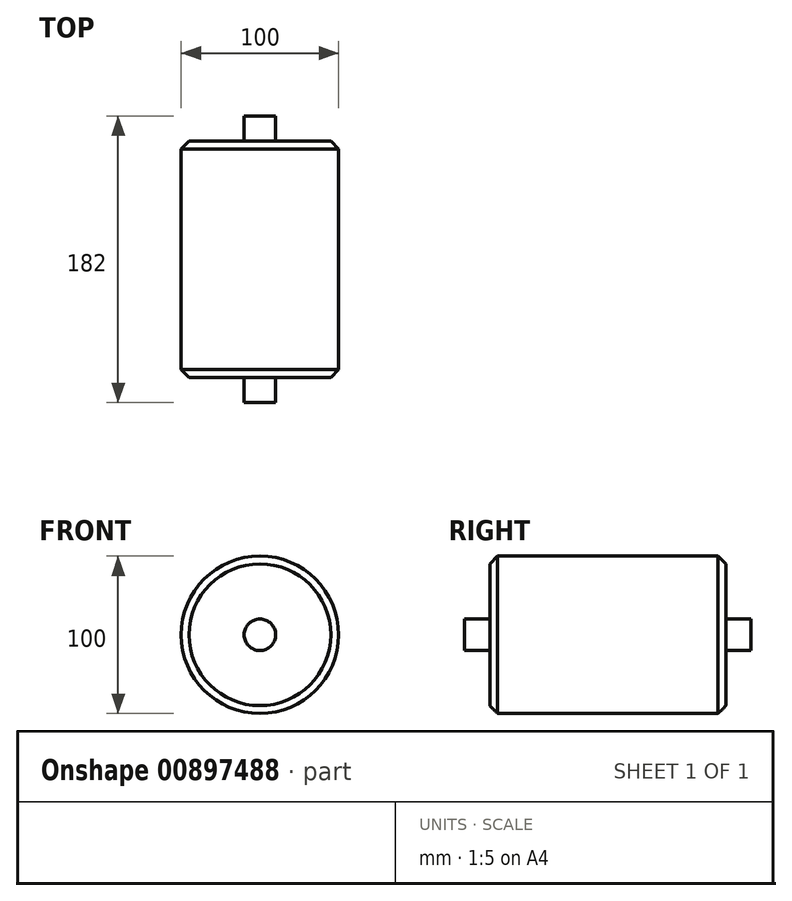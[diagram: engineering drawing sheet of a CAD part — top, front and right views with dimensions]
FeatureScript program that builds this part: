
annotation { "Feature Type Name" : "Feature", "Feature Type Description" : "" }
export const myFeature = defineFeature(function(context is Context, id is Id, definition is map)
    precondition{}
    {
        {
            var Q0;
            Q0=qCreatedBy(makeId("Front.planeOp"),FACE);
            var sketch = newSketch(context, id + "F0", { "sketchPlane" : qUnion([Q0])});
            skCircle(sketch, "E0", {"center": v(0, 0) * mm, "radius": 50 * mm});
            skSolve(sketch);
        }
        {
            var Q0;
            Q0=makeQuery(id+"F0.imprint","IMPRINT",FACE,{"disambiguationData":[TD([[makeQuery(id+"F0.imprint","IMPRINT",EDGE,{"derivedFrom":sQuery(id+"F0.wireOp",EDGE,"E0")}),1.0]])]});
            extrude(context, id + "F1", {"entities" : qUnion([Q0]), "depth" : 150 * mm, "offsetDistance" : 25.4 * mm});
        }
        {
            var Q0;
            Q0=makeQuery(id+"F1.opExtrude","CAP_FACE",FACE,{"disambiguationData":[OSD([sQuery(id+"F0.wireOp",EDGE,"E0")])],"isStart":false});
            var sketch = newSketch(context, id + "F2", { "sketchPlane" : qUnion([Q0])});
            skCircle(sketch, "E1", {"center": v(0, 0) * mm, "radius": 10 * mm});
            skSolve(sketch);
        }
        {
            var Q0;
            Q0 = qSketchRegion(id + "F2", true);
            extrude(context, id + "F3", {"entities" : qUnion([Q0]), "operationType" : NewBodyOperationType.ADD, "depth" : 16 * mm, "offsetDistance" : 25.4 * mm});
        }
        {
            var Q0;
            Q0=makeQuery(id+"F1.opExtrude","CAP_FACE",FACE,{"disambiguationData":[OSD([sQuery(id+"F0.wireOp",EDGE,"E0")])],"isStart":true});
            var sketch = newSketch(context, id + "F4", { "sketchPlane" : qUnion([Q0])});
            skCircle(sketch, "E2", {"center": v(0, 0) * mm, "radius": 10 * mm});
            skSolve(sketch);
        }
        {
            var Q0;
            Q0 = qSketchRegion(id + "F4", true);
            extrude(context, id + "F5", {"entities" : qUnion([Q0]), "operationType" : NewBodyOperationType.ADD, "depth" : 16 * mm, "offsetDistance" : 25.4 * mm});
        }
        {
            var Q0;
            Q0=makeQuery(id+"F1.opExtrude","CAP_EDGE",EDGE,{"disambiguationData":[OSD([sQuery(id+"F0.wireOp",EDGE,"E0")])],"isStart":false});
            var Q1;
            Q1=makeQuery(id+"F1.opExtrude","CAP_EDGE",EDGE,{"disambiguationData":[OSD([sQuery(id+"F0.wireOp",EDGE,"E0")])],"isStart":true});
            chamfer(context, id + "F6", {"entities" : qUnion([Q0, Q1]), "chamferType" : ChamferType.OFFSET_ANGLE, "width" : 5 * mm, "oppositeDirection" : false, "angle" : 45 * degree, "tangentPropagation" : true});
        }
    });
